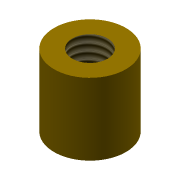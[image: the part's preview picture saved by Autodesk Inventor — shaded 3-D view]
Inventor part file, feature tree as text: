
AUTODESK INVENTOR PART (.ipt)
format: ipt  version: 2022 (Build 260153000, 153)  size: 82,432 bytes
history: native  units: mm
features: sketch x2, extrude x1, hole x1
ambient origin geometry x8: Origin, YZ Plane, XZ Plane, XY Plane, X Axis, Y Axis, Z Axis, Center Point
bodies: Solid1 (feature_tree)
feature tree (4):
  extrude  "Extrusion1"  Depth=5.0mm TaperAngle=0.0deg
  hole  "Hole1"  [1 undecoded]
  sketch  "Sketch1"  dims[d0=5.0mm d1=5.0mm d2=0.0mm]
  sketch  "Sketch2"  dims[d3=2.459mm d4=10.0mm d5=4.0mm d6=2.0mm d7=90.0deg d8=8.0mm d9=20.594885mm]
note: 1 required parameter value undecoded (feature->parameter linkage not recoverable at this tier; creation-order binding heuristic only, values carry confidence <= 0.55)
